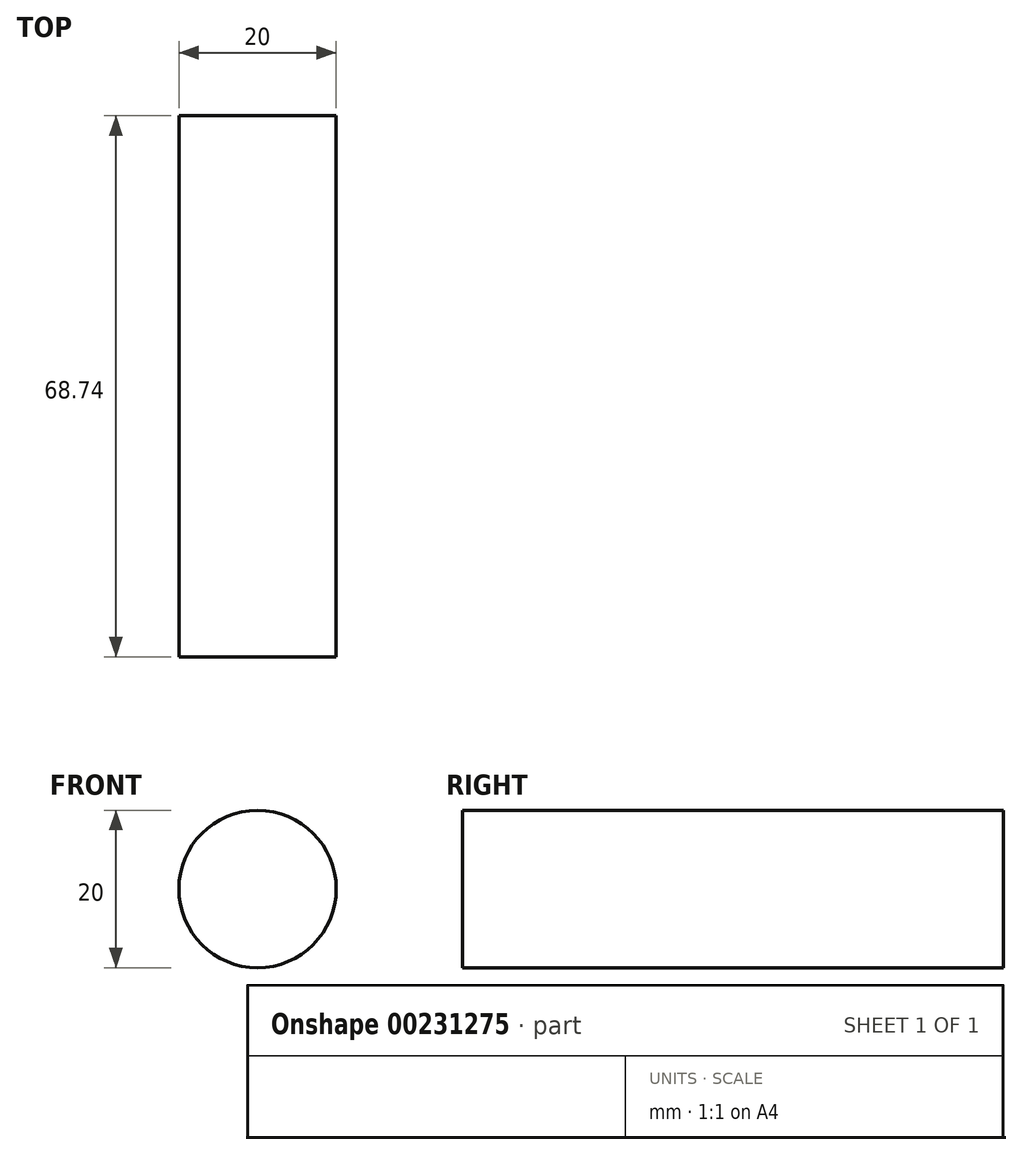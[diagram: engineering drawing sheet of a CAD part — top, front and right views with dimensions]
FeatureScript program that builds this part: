
annotation { "Feature Type Name" : "Feature", "Feature Type Description" : "" }
export const myFeature = defineFeature(function(context is Context, id is Id, definition is map)
    precondition{}
    {
        {
            var Q0;
            Q0=qCreatedBy(makeId("Front.planeOp"),FACE);
            var sketch = newSketch(context, id + "F0", { "sketchPlane" : qUnion([Q0])});
            skCircle(sketch, "E0", {"center": v(0, 0) * mm, "radius": 10 * mm});
            skSolve(sketch);
        }
        {
            var Q0;
            Q0=makeQuery(id+"F0.imprint","IMPRINT",FACE,{"disambiguationData":[TD([[makeQuery(id+"F0.imprint","IMPRINT",EDGE,{"derivedFrom":sQuery(id+"F0.wireOp",EDGE,"E0")}),1.0]])]});
            extrude(context, id + "F1", {"entities" : qUnion([Q0]), "depth" : (70 - 1.28 + 0.02) * mm});
        }
    });
